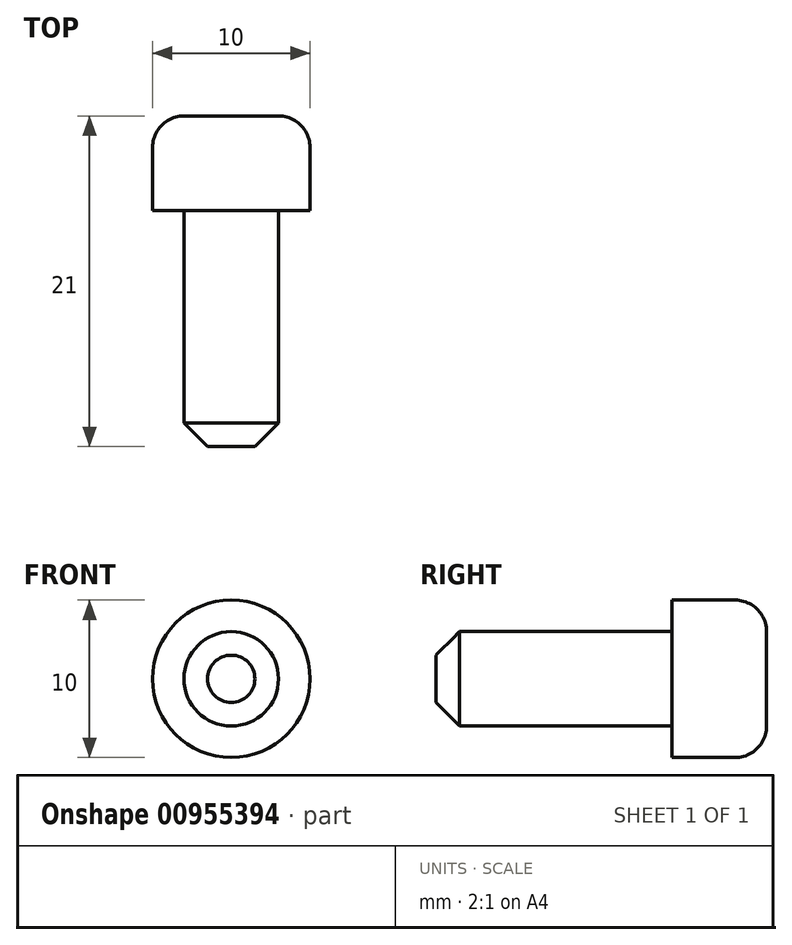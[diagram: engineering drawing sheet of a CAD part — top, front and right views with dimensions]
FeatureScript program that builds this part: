
annotation { "Feature Type Name" : "Feature", "Feature Type Description" : "" }
export const myFeature = defineFeature(function(context is Context, id is Id, definition is map)
    precondition{}
    {
        {
            var Q0;
            Q0=qCreatedBy(makeId("Right.planeOp"),FACE);
            var sketch = newSketch(context, id + "F0", { "sketchPlane" : qUnion([Q0])});
            skLineSegment(sketch, "E0", {"start": v(17.04, 0) * mm, "end": v(17.04, 5) * mm});
            skLineSegment(sketch, "E1", {"start": v(17.04, 5) * mm, "end": v(11.04, 5) * mm});
            skLineSegment(sketch, "E2", {"start": v(11.04, 5) * mm, "end": v(11.04, 3) * mm});
            skLineSegment(sketch, "E3", {"start": v(11.04, 3) * mm, "end": v(-3.96, 3) * mm});
            skLineSegment(sketch, "E4", {"start": v(-3.96, 3) * mm, "end": v(-3.96, 0) * mm});
            skLineSegment(sketch, "E5", {"start": v(-3.96, 0) * mm, "end": v(17.04, 0) * mm});
            skSolve(sketch);
        }
        {
            var Q0;
            Q0=qSketchRegion(id+"F0",true);
            var Q1;
            Q1=sQuery(id+"F0.wireOp",EDGE,"E5");
            revolve(context, id + "F1", {"entities" : qUnion([Q0]), "axis" : qUnion([Q1]), "revolveType" : RevolveType.FULL});
        }
        {
            var Q0;
            Q0=makeQuery(id+"F1.opRevolve","SWEPT_EDGE",EDGE,{"disambiguationData":[OSD([sQuery(id+"F0.wireOp",EDGE,"E3"),sQuery(id+"F0.wireOp",EDGE,"E4")])]});
            chamfer(context, id + "F2", {"entities" : qUnion([Q0]), "width" : 1.5 * mm, "tangentPropagation" : true});
        }
        {
            var Q0;
            Q0=makeQuery(id+"F1.opRevolve","SWEPT_EDGE",EDGE,{"disambiguationData":[OSD([sQuery(id+"F0.wireOp",EDGE,"E0"),sQuery(id+"F0.wireOp",EDGE,"E1")])]});
            fillet(context, id + "F3", {"entities" : qUnion([Q0]), "radius" : 2 * mm, "tangentPropagation" : true, "allowEdgeOverflow" : false});
        }
    });
